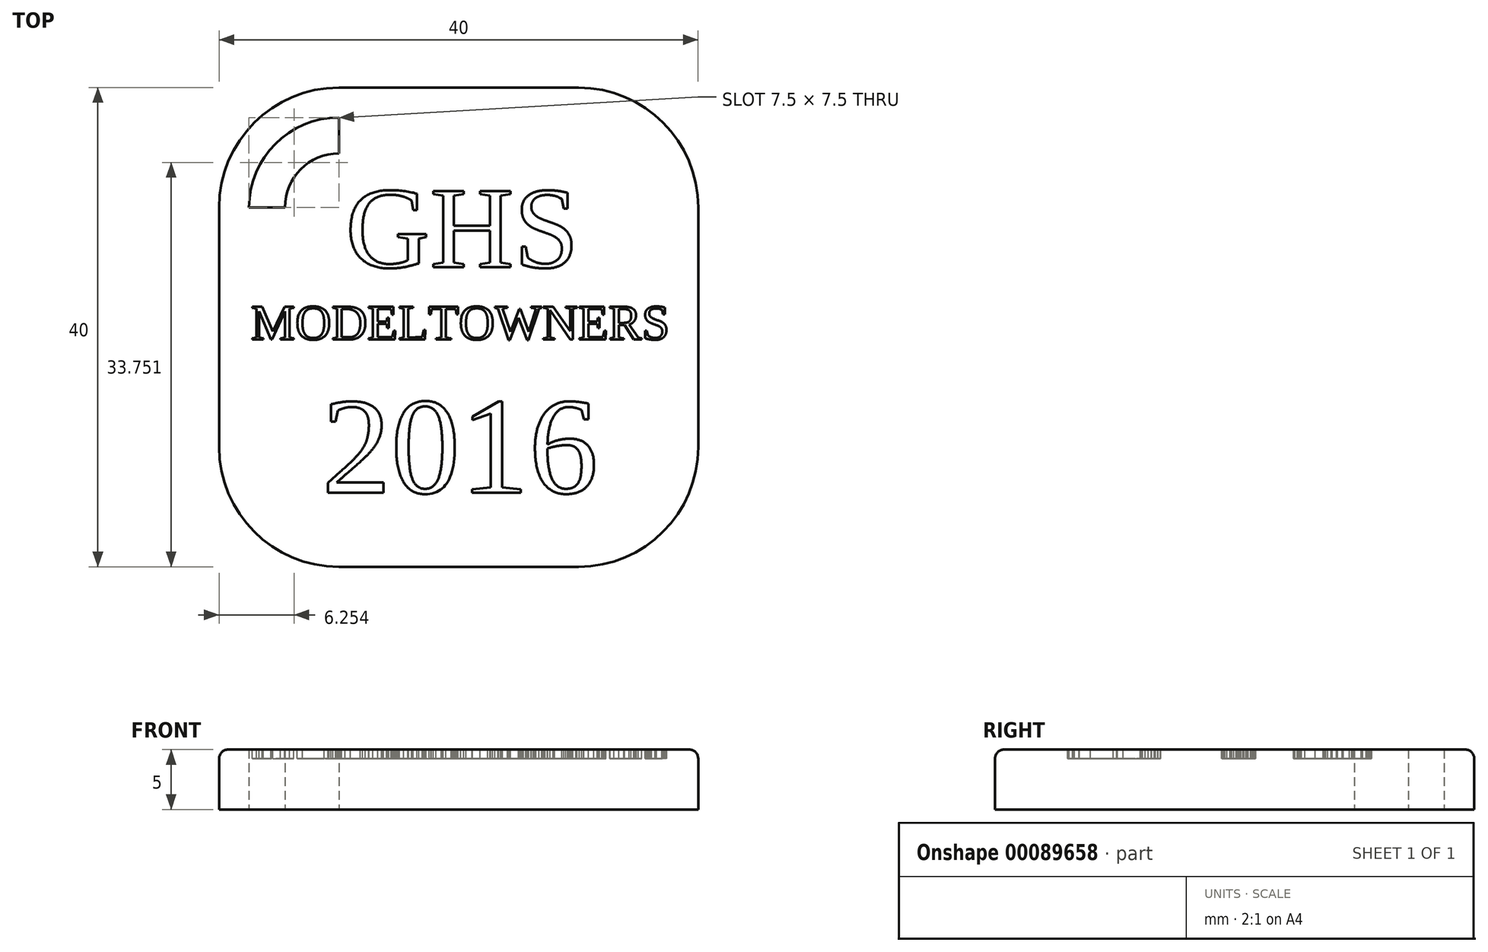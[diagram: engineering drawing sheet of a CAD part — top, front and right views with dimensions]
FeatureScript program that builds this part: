
annotation { "Feature Type Name" : "Feature", "Feature Type Description" : "" }
export const myFeature = defineFeature(function(context is Context, id is Id, definition is map)
    precondition{}
    {
        {
            var Q0;
            Q0=qCreatedBy(makeId("Top.planeOp"),FACE);
            var sketch = newSketch(context, id + "F0", { "sketchPlane" : qUnion([Q0])});
            skLineSegment(sketch, "E0.bottom", {"start": v(-73.67, 40.7) * mm, "end": v(-53.67, 40.7) * mm});
            skLineSegment(sketch, "E0.top", {"start": v(-73.67, 0.7) * mm, "end": v(-53.67, 0.7) * mm});
            skLineSegment(sketch, "E0.left", {"start": v(-83.67, 30.7) * mm, "end": v(-83.67, 10.7) * mm});
            skLineSegment(sketch, "E0.right", {"start": v(-43.67, 30.7) * mm, "end": v(-43.67, 10.7) * mm});
            skPoint(sketch, "E1.visualSharp", {"position": v(-83.67, 40.7) * mm});
            skArc(sketch, "E1.filletArc", {"start": v(-73.67, 40.7) * mm, "mid": v(-80.74, 37.77) * mm, "end": v(-83.67, 30.7) * mm});
            skPoint(sketch, "E2.visualSharp", {"position": v(-43.67, 40.7) * mm});
            skArc(sketch, "E2.filletArc", {"start": v(-43.67, 30.7) * mm, "mid": v(-46.6, 37.77) * mm, "end": v(-53.67, 40.7) * mm});
            skPoint(sketch, "E3.visualSharp", {"position": v(-43.67, 0.7) * mm});
            skArc(sketch, "E3.filletArc", {"start": v(-53.67, 0.7) * mm, "mid": v(-46.6, 3.63) * mm, "end": v(-43.67, 10.7) * mm});
            skPoint(sketch, "E4.visualSharp", {"position": v(-83.67, 0.7) * mm});
            skArc(sketch, "E4.filletArc", {"start": v(-83.67, 10.7) * mm, "mid": v(-80.74, 3.63) * mm, "end": v(-73.67, 0.7) * mm});
            skPoint(sketch, "E5.visualSharp", {"position": v(-81.17, 38.2) * mm});
            skArc(sketch, "E5.filletArc", {"start": v(-73.67, 38.2) * mm, "mid": v(-78.97, 36) * mm, "end": v(-81.17, 30.7) * mm});
            skArc(sketch, "E6.1", {"start": v(-73.67, 35.2) * mm, "mid": v(-76.85, 33.88) * mm, "end": v(-78.17, 30.7) * mm});
            skLineSegment(sketch, "E7", {"start": v(-73.67, 38.2) * mm, "end": v(-73.67, 35.2) * mm});
            skLineSegment(sketch, "E8", {"start": v(-78.17, 30.7) * mm, "end": v(-81.17, 30.7) * mm});
            skSolve(sketch);
        }
        {
            var Q0;
            Q0=qSketchRegion(id+"F0",true);
            extrude(context, id + "F1", {"entities" : qUnion([Q0]), "depth" : 5 * mm});
        }
        {
            var Q0;
            Q0=makeQuery(id+"F1.opExtrude","CAP_FACE",FACE,{"disambiguationData":[OSD([sQuery(id+"F0.wireOp",EDGE,"E0.bottom"),sQuery(id+"F0.wireOp",EDGE,"E0.top"),sQuery(id+"F0.wireOp",EDGE,"E0.left"),sQuery(id+"F0.wireOp",EDGE,"E0.right"),sQuery(id+"F0.wireOp",EDGE,"E1.filletArc"),sQuery(id+"F0.wireOp",EDGE,"E2.filletArc"),sQuery(id+"F0.wireOp",EDGE,"E3.filletArc"),sQuery(id+"F0.wireOp",EDGE,"E4.filletArc"),sQuery(id+"F0.wireOp",EDGE,"E5.filletArc"),sQuery(id+"F0.wireOp",EDGE,"E6.1"),sQuery(id+"F0.wireOp",EDGE,"E7"),sQuery(id+"F0.wireOp",EDGE,"E8")])],"isStart":false});
            var sketch = newSketch(context, id + "F2", { "sketchPlane" : qUnion([Q0])});
            skPoint(sketch, "E9.centerSnap0", {"position": v(-63.67, 40.7) * mm});
            skPoint(sketch, "E9.centerSnap1", {"position": v(-43.67, 20.7) * mm});
            skText(sketch, "E10", { "text": "GHS", "fontName": "Tinos-Regular.ttf"});
            skText(sketch, "E11", { "text": "MODELTOWNERS", "fontName": "Tinos-Regular.ttf"});
            skText(sketch, "E12", { "text": "2016", "fontName": "Tinos-Regular.ttf"});
            const initialGuessF2  = {"E10": [-0.07309, 0.0257, 1, 0, 0.007], "E11": [-0.08101, 0.01968, 1, 0, 0.003], "E12": [-0.07508, 0.00688, 1, 0, 0.0083]};
            skSetInitialGuess(sketch, initialGuessF2);
            skSolve(sketch);
        }
        {
            var Q0;
            Q0=makeQuery(id+"F1.opExtrude","CAP_EDGE",EDGE,{"disambiguationData":[OSD([sQuery(id+"F0.wireOp",EDGE,"E0.left")])],"isStart":false});
            var Q1;
            Q1=makeQuery(id+"F1.opExtrude","CAP_EDGE",EDGE,{"disambiguationData":[OSD([sQuery(id+"F0.wireOp",EDGE,"E4.filletArc")])],"isStart":false});
            var Q2;
            Q2=makeQuery(id+"F1.opExtrude","CAP_EDGE",EDGE,{"disambiguationData":[OSD([sQuery(id+"F0.wireOp",EDGE,"E0.top")])],"isStart":false});
            var Q3;
            Q3=makeQuery(id+"F1.opExtrude","CAP_EDGE",EDGE,{"disambiguationData":[OSD([sQuery(id+"F0.wireOp",EDGE,"E3.filletArc")])],"isStart":false});
            var Q4;
            Q4=makeQuery(id+"F1.opExtrude","CAP_EDGE",EDGE,{"disambiguationData":[OSD([sQuery(id+"F0.wireOp",EDGE,"E0.right")])],"isStart":false});
            var Q5;
            Q5=makeQuery(id+"F1.opExtrude","CAP_EDGE",EDGE,{"disambiguationData":[OSD([sQuery(id+"F0.wireOp",EDGE,"E2.filletArc")])],"isStart":false});
            var Q6;
            Q6=makeQuery(id+"F1.opExtrude","CAP_EDGE",EDGE,{"disambiguationData":[OSD([sQuery(id+"F0.wireOp",EDGE,"E0.bottom")])],"isStart":false});
            var Q7;
            Q7=makeQuery(id+"F1.opExtrude","CAP_EDGE",EDGE,{"disambiguationData":[OSD([sQuery(id+"F0.wireOp",EDGE,"E1.filletArc")])],"isStart":false});
            fillet(context, id + "F3", {"entities" : qUnion([Q0, Q1, Q2, Q3, Q4, Q5, Q6, Q7]), "radius" : 0.75 * mm, "tangentPropagation" : true, "allowEdgeOverflow" : false});
        }
        {
            var Q0;
            Q0 = qSketchRegion(id + "F2", true);
            extrude(context, id + "F4", {"entities" : qUnion([Q0]), "operationType" : NewBodyOperationType.REMOVE, "oppositeDirection" : true, "depth" : 0.75 * mm});
        }
    });
